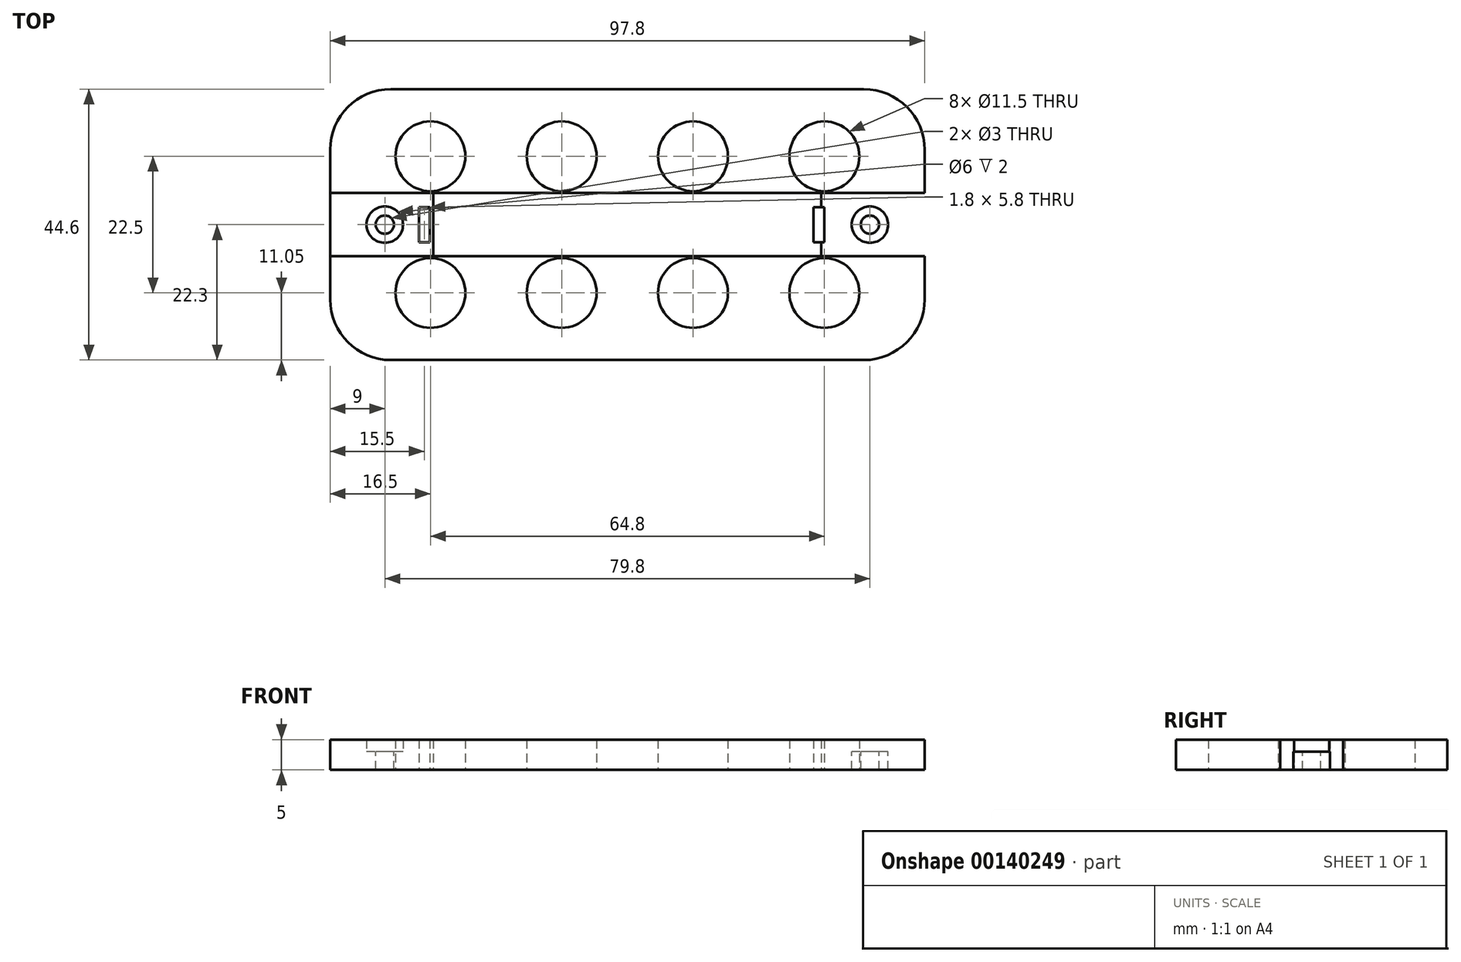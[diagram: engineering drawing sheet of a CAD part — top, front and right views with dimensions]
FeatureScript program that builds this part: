
annotation { "Feature Type Name" : "Feature", "Feature Type Description" : "" }
export const myFeature = defineFeature(function(context is Context, id is Id, definition is map)
    precondition{}
    {
        {
            var Q0;
            Q0=qCreatedBy(makeId("Top.planeOp"),FACE);
            var sketch = newSketch(context, id + "F0", { "sketchPlane" : qUnion([Q0])});
            skLineSegment(sketch, "E0", {"start": v(-3.6, 10.25) * mm, "end": v(18, 10.25) * mm});
            skLineSegment(sketch, "E1", {"start": v(-3.6, 10.25) * mm, "end": v(-25.2, 10.25) * mm});
            skLineSegment(sketch, "E2", {"start": v(-3.6, 0) * mm, "end": v(-3.6, -10.25) * mm});
            skLineSegment(sketch, "E3", {"start": v(-3.6, -10.25) * mm, "end": v(-25.2, -10.25) * mm});
            skLineSegment(sketch, "E4", {"start": v(-3.6, -10.25) * mm, "end": v(18, -10.25) * mm});
            skLineSegment(sketch, "E5.0", {"start": v(-3.6, 11.25) * mm, "end": v(-25.2, 11.25) * mm});
            skLineSegment(sketch, "E5.1", {"start": v(-3.6, 11.25) * mm, "end": v(18, 11.25) * mm});
            skLineSegment(sketch, "E6.0", {"start": v(-3.6, -11.25) * mm, "end": v(18, -11.25) * mm});
            skLineSegment(sketch, "E6.1", {"start": v(-3.6, -11.25) * mm, "end": v(-25.2, -11.25) * mm});
            skLineSegment(sketch, "E7", {"start": v(18, -11.25) * mm, "end": v(39.6, -11.25) * mm});
            skLineSegment(sketch, "E8", {"start": v(18, 11.25) * mm, "end": v(39.6, 11.25) * mm});
            skLineSegment(sketch, "E9", {"start": v(7.2, 11.25) * mm, "end": v(7.2, 0) * mm});
            skLineSegment(sketch, "E10.bottom", {"start": v(-41.7, 22.3) * mm, "end": v(56.1, 22.3) * mm});
            skLineSegment(sketch, "E10.top", {"start": v(-41.7, -22.3) * mm, "end": v(56.1, -22.3) * mm});
            skLineSegment(sketch, "E10.left", {"start": v(-41.7, 22.3) * mm, "end": v(-41.7, -22.3) * mm});
            skLineSegment(sketch, "E10.right", {"start": v(56.1, 22.3) * mm, "end": v(56.1, -22.3) * mm});
            skPoint(sketch, "E10.middle", {"position": v(7.2, 0) * mm});
            skCircle(sketch, "E11", {"center": v(-25.2, 11.25) * mm, "radius": 5.75 * mm});
            skCircle(sketch, "E12", {"center": v(-3.6, 11.25) * mm, "radius": 5.75 * mm});
            skCircle(sketch, "E13", {"center": v(18, 11.25) * mm, "radius": 5.75 * mm});
            skCircle(sketch, "E14", {"center": v(39.6, 11.25) * mm, "radius": 5.75 * mm});
            skCircle(sketch, "E15", {"center": v(-25.2, -11.25) * mm, "radius": 5.75 * mm});
            skCircle(sketch, "E16", {"center": v(-3.6, -11.25) * mm, "radius": 5.75 * mm});
            skCircle(sketch, "E17", {"center": v(18, -11.25) * mm, "radius": 5.75 * mm});
            skCircle(sketch, "E18", {"center": v(39.6, -11.25) * mm, "radius": 5.75 * mm});
            skLineSegment(sketch, "E19", {"start": v(56.1, 0) * mm, "end": v(56.1, -5.2) * mm});
            skLineSegment(sketch, "E20", {"start": v(56.1, 0) * mm, "end": v(56.1, 5.2) * mm});
            skLineSegment(sketch, "E21", {"start": v(56.1, 5.2) * mm, "end": v(-41.7, 5.2) * mm});
            skLineSegment(sketch, "E22", {"start": v(56.1, -5.2) * mm, "end": v(-41.7, -5.2) * mm});
            skLineSegment(sketch, "E23", {"start": v(-41.7, 0) * mm, "end": v(-32.7, 0) * mm});
            skCircle(sketch, "E24", {"center": v(-32.7, 0) * mm, "radius": 3 * mm});
            skCircle(sketch, "E25", {"center": v(-32.7, 0) * mm, "radius": 1.5 * mm});
            skLineSegment(sketch, "E26", {"start": v(56.1, 0) * mm, "end": v(47.1, 0) * mm});
            skCircle(sketch, "E27", {"center": v(47.1, 0) * mm, "radius": 3 * mm});
            skCircle(sketch, "E28", {"center": v(47.1, 0) * mm, "radius": 1.5 * mm});
            skLineSegment(sketch, "E29", {"start": v(-41.7, -5.2) * mm, "end": v(-25.2, -5.2) * mm});
            skLineSegment(sketch, "E30", {"start": v(56.1, 5.2) * mm, "end": v(39.6, 5.2) * mm});
            skLineSegment(sketch, "E31", {"start": v(-41.7, -5.2) * mm, "end": v(-24.7, -5.2) * mm});
            skLineSegment(sketch, "E32", {"start": v(-24.7, -5.2) * mm, "end": v(-24.7, 5.2) * mm});
            skLineSegment(sketch, "E33", {"start": v(56.1, -5.2) * mm, "end": v(39.1, -5.2) * mm});
            skLineSegment(sketch, "E34", {"start": v(39.1, -5.2) * mm, "end": v(39.1, 5.2) * mm});
            skLineSegment(sketch, "E35", {"start": v(-41.7, 0) * mm, "end": v(-27.1, 0) * mm});
            skLineSegment(sketch, "E36", {"start": v(-27.1, 0) * mm, "end": v(-27.1, 2.9) * mm});
            skLineSegment(sketch, "E37", {"start": v(-27.1, 2.9) * mm, "end": v(-25.3, 2.9) * mm});
            skLineSegment(sketch, "E38", {"start": v(-25.3, 2.9) * mm, "end": v(-25.3, -2.9) * mm});
            skLineSegment(sketch, "E39", {"start": v(-25.3, -2.9) * mm, "end": v(-27.1, -2.9) * mm});
            skLineSegment(sketch, "E40", {"start": v(-27.1, -2.9) * mm, "end": v(-27.1, 0) * mm});
            skLineSegment(sketch, "E41", {"start": v(56.1, 0) * mm, "end": v(39.6, 0) * mm});
            skLineSegment(sketch, "E42", {"start": v(39.6, 0) * mm, "end": v(39.6, 2.9) * mm});
            skLineSegment(sketch, "E43", {"start": v(39.6, 2.9) * mm, "end": v(37.8, 2.9) * mm});
            skLineSegment(sketch, "E44", {"start": v(37.8, 2.9) * mm, "end": v(37.8, -2.9) * mm});
            skLineSegment(sketch, "E45", {"start": v(37.8, -2.9) * mm, "end": v(39.6, -2.9) * mm});
            skLineSegment(sketch, "E46", {"start": v(39.6, -2.9) * mm, "end": v(39.6, 0) * mm});
            skSolve(sketch);
        }
        {
            var Q0;
            Q0=makeQuery(id+"F0.imprint","IMPRINT",FACE,{"disambiguationData":[TD([[makeQuery(id+"F0.imprint","IMPRINT",EDGE,{"derivedFrom":sQuery(id+"F0.wireOp",EDGE,"E10.bottom")}),-1.0]])]});
            var Q1;
            {var subQ0=sQuery(id+"F0.wireOp",EDGE,"f6887ee9-049f-47f7-8b07-7ff9263f95ff");var subQ1=makeQuery(id+"F0.imprint","INTERSECT",VERTEX,{"derivedFrom":[sQuery(id+"F0.wireOp",EDGE,"E3"),subQ0]});Q1=makeQuery(id+"F0.imprint","IMPRINT",FACE,{"disambiguationData":[TD([[makeQuery(id+"F0.imprint","IMPRINT",EDGE,{"disambiguationData":[TD([[subQ1,-1.0]])],"derivedFrom":subQ0}),1.0]])]});}
            var Q2;
            {var subQ0=sQuery(id+"F0.wireOp",EDGE,"7b2065db-7b24-4620-b89c-c6dd7d309109");var subQ1=makeQuery(id+"F0.imprint","INTERSECT",VERTEX,{"derivedFrom":[sQuery(id+"F0.wireOp",EDGE,"E1"),subQ0]});Q2=makeQuery(id+"F0.imprint","IMPRINT",FACE,{"disambiguationData":[TD([[makeQuery(id+"F0.imprint","IMPRINT",EDGE,{"disambiguationData":[TD([[subQ1,-1.0]])],"derivedFrom":subQ0}),1.0]])]});}
            var Q3;
            {var subQ1=sQuery(id+"F0.wireOp",EDGE,"4b9a3b46-39bf-4a7f-935b-aec41dfed67a");var subQ3=sQuery(id+"F0.wireOp",EDGE,"3ee279bb-5b09-4dd3-93a1-242deb24ec6a");var subQ4=makeQuery(id+"F0.imprint","INTERSECT",VERTEX,{"derivedFrom":[subQ1,subQ3]});Q3=makeQuery(id+"F0.imprint","IMPRINT",FACE,{"disambiguationData":[TD([[makeQuery(id+"F0.imprint","IMPRINT",EDGE,{"disambiguationData":[TD([[subQ4,1.0]])],"derivedFrom":subQ3}),1.0]])]});}
            var Q4;
            {var subQ0=sQuery(id+"F0.wireOp",EDGE,"4c88f515-e4cd-4761-96bb-9e012f7b4129");var subQ1=makeQuery(id+"F0.imprint","INTERSECT",VERTEX,{"derivedFrom":[sQuery(id+"F0.wireOp",EDGE,"E0"),subQ0]});Q4=makeQuery(id+"F0.imprint","IMPRINT",FACE,{"disambiguationData":[TD([[makeQuery(id+"F0.imprint","IMPRINT",EDGE,{"disambiguationData":[TD([[subQ1,1.0]])],"derivedFrom":subQ0}),1.0]])]});}
            var Q5;
            {var subQ0=sQuery(id+"F0.wireOp",EDGE,"98f43cb8-49ac-4cd2-891b-843e99cd508c");var subQ1=makeQuery(id+"F0.imprint","INTERSECT",VERTEX,{"derivedFrom":[sQuery(id+"F0.wireOp",EDGE,"E4"),subQ0]});Q5=makeQuery(id+"F0.imprint","IMPRINT",FACE,{"disambiguationData":[TD([[makeQuery(id+"F0.imprint","IMPRINT",EDGE,{"disambiguationData":[TD([[subQ1,-1.0]])],"derivedFrom":subQ0}),1.0]])]});}
            var Q6;
            {var subQ1=sQuery(id+"F0.wireOp",EDGE,"4b9a3b46-39bf-4a7f-935b-aec41dfed67a");var subQ3=sQuery(id+"F0.wireOp",EDGE,"3ee279bb-5b09-4dd3-93a1-242deb24ec6a");var subQ4=makeQuery(id+"F0.imprint","INTERSECT",VERTEX,{"derivedFrom":[subQ1,subQ3]});Q6=makeQuery(id+"F0.imprint","IMPRINT",FACE,{"disambiguationData":[TD([[makeQuery(id+"F0.imprint","IMPRINT",EDGE,{"disambiguationData":[TD([[subQ4,-1.0]])],"derivedFrom":subQ3}),1.0]])]});}
            var Q7;
            {var subQ3=sQuery(id+"F0.wireOp",EDGE,"3ee279bb-5b09-4dd3-93a1-242deb24ec6a");var subQ5=sQuery(id+"F0.wireOp",EDGE,"E5.1");var subQ8=makeQuery(id+"F0.imprint","INTERSECT",VERTEX,{"derivedFrom":[subQ3,subQ5]});Q7=makeQuery(id+"F0.imprint","IMPRINT",FACE,{"disambiguationData":[TD([[makeQuery(id+"F0.imprint","IMPRINT",EDGE,{"disambiguationData":[TD([[subQ8,1.0]])],"derivedFrom":subQ3}),1.0]])]});}
            var Q8;
            {var subQ0=sQuery(id+"F0.wireOp",EDGE,"E5.1");var subQ1=sQuery(id+"F0.wireOp",EDGE,"3ee279bb-5b09-4dd3-93a1-242deb24ec6a");var subQ2=makeQuery(id+"F0.imprint","INTERSECT",VERTEX,{"derivedFrom":[subQ1,subQ0]});Q8=makeQuery(id+"F0.imprint","IMPRINT",FACE,{"disambiguationData":[TD([[makeQuery(id+"F0.imprint","IMPRINT",EDGE,{"disambiguationData":[TD([[subQ2,-1.0]])],"derivedFrom":subQ1}),1.0]])]});}
            var Q9;
            {var subQ0=sQuery(id+"F0.wireOp",EDGE,"E8");var subQ1=sQuery(id+"F0.wireOp",EDGE,"4c88f515-e4cd-4761-96bb-9e012f7b4129");var subQ2=makeQuery(id+"F0.imprint","INTERSECT",VERTEX,{"derivedFrom":[subQ1,subQ0]});Q9=makeQuery(id+"F0.imprint","IMPRINT",FACE,{"disambiguationData":[TD([[makeQuery(id+"F0.imprint","IMPRINT",EDGE,{"disambiguationData":[TD([[subQ2,-1.0]])],"derivedFrom":subQ1}),1.0]])]});}
            var Q10;
            {var subQ0=sQuery(id+"F0.wireOp",EDGE,"E6.1");var subQ1=sQuery(id+"F0.wireOp",EDGE,"78d3df8a-ec91-46e3-93df-5ccd42c28f7d");var subQ2=makeQuery(id+"F0.imprint","INTERSECT",VERTEX,{"derivedFrom":[subQ1,subQ0]});Q10=makeQuery(id+"F0.imprint","IMPRINT",FACE,{"disambiguationData":[TD([[makeQuery(id+"F0.imprint","IMPRINT",EDGE,{"disambiguationData":[TD([[subQ2,-1.0]])],"derivedFrom":subQ1}),1.0]])]});}
            var Q11;
            {var subQ0=sQuery(id+"F0.wireOp",EDGE,"E7");var subQ1=sQuery(id+"F0.wireOp",EDGE,"98f43cb8-49ac-4cd2-891b-843e99cd508c");var subQ2=makeQuery(id+"F0.imprint","INTERSECT",VERTEX,{"derivedFrom":[subQ1,subQ0]});Q11=makeQuery(id+"F0.imprint","IMPRINT",FACE,{"disambiguationData":[TD([[makeQuery(id+"F0.imprint","IMPRINT",EDGE,{"disambiguationData":[TD([[subQ2,1.0]])],"derivedFrom":subQ1}),1.0]])]});}
            var Q12;
            {var subQ0=sQuery(id+"F0.wireOp",EDGE,"E9");var subQ1=sQuery(id+"F0.wireOp",EDGE,"E0");var subQ2=makeQuery(id+"F0.imprint","INTERSECT",VERTEX,{"derivedFrom":[subQ1,subQ0]});Q12=makeQuery(id+"F0.imprint","IMPRINT",FACE,{"disambiguationData":[TD([[makeQuery(id+"F0.imprint","IMPRINT",EDGE,{"disambiguationData":[TD([[subQ2,-1.0]])],"derivedFrom":subQ1}),1.0]])]});}
            var Q13;
            {var subQ1=sQuery(id+"F0.wireOp",EDGE,"E2");var subQ3=sQuery(id+"F0.wireOp",EDGE,"78d3df8a-ec91-46e3-93df-5ccd42c28f7d");var subQ4=makeQuery(id+"F0.imprint","INTERSECT",VERTEX,{"derivedFrom":[subQ1,subQ3]});Q13=makeQuery(id+"F0.imprint","IMPRINT",FACE,{"disambiguationData":[TD([[makeQuery(id+"F0.imprint","IMPRINT",EDGE,{"disambiguationData":[TD([[subQ4,-1.0]])],"derivedFrom":subQ3}),1.0]])]});}
            var Q14;
            {var subQ0=sQuery(id+"F0.wireOp",EDGE,"E9");var subQ1=sQuery(id+"F0.wireOp",EDGE,"E0");var subQ2=makeQuery(id+"F0.imprint","INTERSECT",VERTEX,{"derivedFrom":[subQ1,subQ0]});Q14=makeQuery(id+"F0.imprint","IMPRINT",FACE,{"disambiguationData":[TD([[makeQuery(id+"F0.imprint","IMPRINT",EDGE,{"disambiguationData":[TD([[subQ2,-1.0]])],"derivedFrom":subQ1}),1.0]])]});}
            var Q15;
            {var subQ0=sQuery(id+"F0.wireOp",EDGE,"E5.1");var subQ1=sQuery(id+"F0.wireOp",EDGE,"3ee279bb-5b09-4dd3-93a1-242deb24ec6a");var subQ2=makeQuery(id+"F0.imprint","INTERSECT",VERTEX,{"derivedFrom":[subQ1,subQ0]});Q15=makeQuery(id+"F0.imprint","IMPRINT",FACE,{"disambiguationData":[TD([[makeQuery(id+"F0.imprint","IMPRINT",EDGE,{"disambiguationData":[TD([[subQ2,1.0]])],"derivedFrom":subQ1}),-1.0]])]});}
            var Q16;
            {var subQ0=sQuery(id+"F0.wireOp",EDGE,"E5.0");var subQ1=sQuery(id+"F0.wireOp",EDGE,"3ee279bb-5b09-4dd3-93a1-242deb24ec6a");var subQ2=makeQuery(id+"F0.imprint","INTERSECT",VERTEX,{"derivedFrom":[subQ1,subQ0]});Q16=makeQuery(id+"F0.imprint","IMPRINT",FACE,{"disambiguationData":[TD([[makeQuery(id+"F0.imprint","IMPRINT",EDGE,{"disambiguationData":[TD([[subQ2,-1.0]])],"derivedFrom":subQ1}),-1.0]])]});}
            var Q17;
            {var subQ0=sQuery(id+"F0.wireOp",EDGE,"f6887ee9-049f-47f7-8b07-7ff9263f95ff");var subQ1=sQuery(id+"F0.wireOp",EDGE,"E3");var subQ2=makeQuery(id+"F0.imprint","INTERSECT",VERTEX,{"derivedFrom":[subQ1,subQ0]});Q17=makeQuery(id+"F0.imprint","IMPRINT",FACE,{"disambiguationData":[TD([[makeQuery(id+"F0.imprint","IMPRINT",EDGE,{"disambiguationData":[TD([[subQ2,1.0]])],"derivedFrom":subQ1}),1.0]])]});}
            var Q18;
            {var subQ1=sQuery(id+"F0.wireOp",EDGE,"E2");var subQ3=sQuery(id+"F0.wireOp",EDGE,"78d3df8a-ec91-46e3-93df-5ccd42c28f7d");var subQ4=makeQuery(id+"F0.imprint","INTERSECT",VERTEX,{"derivedFrom":[subQ1,subQ3]});Q18=makeQuery(id+"F0.imprint","IMPRINT",FACE,{"disambiguationData":[TD([[makeQuery(id+"F0.imprint","IMPRINT",EDGE,{"disambiguationData":[TD([[subQ4,1.0]])],"derivedFrom":subQ3}),1.0]])]});}
            var Q19;
            {var subQ0=sQuery(id+"F0.wireOp",EDGE,"78d3df8a-ec91-46e3-93df-5ccd42c28f7d");var subQ5=sQuery(id+"F0.wireOp",EDGE,"E3");var subQ6=makeQuery(id+"F0.imprint","INTERSECT",VERTEX,{"derivedFrom":[subQ5,subQ0]});Q19=makeQuery(id+"F0.imprint","IMPRINT",FACE,{"disambiguationData":[TD([[makeQuery(id+"F0.imprint","IMPRINT",EDGE,{"disambiguationData":[TD([[subQ6,-1.0]])],"derivedFrom":subQ0}),1.0]])]});}
            var Q20;
            {var subQ0=sQuery(id+"F0.wireOp",EDGE,"98f43cb8-49ac-4cd2-891b-843e99cd508c");var subQ1=sQuery(id+"F0.wireOp",EDGE,"E4");var subQ2=makeQuery(id+"F0.imprint","INTERSECT",VERTEX,{"derivedFrom":[subQ1,subQ0]});Q20=makeQuery(id+"F0.imprint","IMPRINT",FACE,{"disambiguationData":[TD([[makeQuery(id+"F0.imprint","IMPRINT",EDGE,{"disambiguationData":[TD([[subQ2,1.0]])],"derivedFrom":subQ1}),-1.0]])]});}
            var Q21;
            {var subQ0=sQuery(id+"F0.wireOp",EDGE,"E9");var subQ1=sQuery(id+"F0.wireOp",EDGE,"E0");var subQ2=makeQuery(id+"F0.imprint","INTERSECT",VERTEX,{"derivedFrom":[subQ1,subQ0]});Q21=makeQuery(id+"F0.imprint","IMPRINT",FACE,{"disambiguationData":[TD([[makeQuery(id+"F0.imprint","IMPRINT",EDGE,{"disambiguationData":[TD([[subQ2,1.0]])],"derivedFrom":subQ1}),1.0]])]});}
            var Q22;
            {var subQ0=sQuery(id+"F0.wireOp",EDGE,"E11");var subQ1=sQuery(id+"F0.wireOp",EDGE,"E1");var subQ2=makeQuery(id+"F0.imprint","INTERSECT",VERTEX,{"derivedFrom":[subQ1,subQ0]});Q22=makeQuery(id+"F0.imprint","IMPRINT",FACE,{"disambiguationData":[TD([[makeQuery(id+"F0.imprint","IMPRINT",EDGE,{"disambiguationData":[TD([[subQ2,1.0]])],"derivedFrom":subQ1}),-1.0]])]});}
            var Q23;
            {var subQ8=sQuery(id+"F0.wireOp",EDGE,"E10.top");Q23=makeQuery(id+"F0.imprint","IMPRINT",FACE,{"disambiguationData":[TD([[makeQuery(id+"F0.imprint","IMPRINT",EDGE,{"derivedFrom":subQ8}),1.0]])]});}
            var Q24;
            {var subQ1=sQuery(id+"F0.wireOp",EDGE,"4b9a3b46-39bf-4a7f-935b-aec41dfed67a");var subQ5=sQuery(id+"F0.wireOp",EDGE,"E21");var subQ9=makeQuery(id+"F0.imprint","INTERSECT",VERTEX,{"derivedFrom":[subQ1,subQ5]});Q24=makeQuery(id+"F0.imprint","IMPRINT",FACE,{"disambiguationData":[TD([[makeQuery(id+"F0.imprint","IMPRINT",EDGE,{"disambiguationData":[TD([[subQ9,-1.0]])],"derivedFrom":subQ1}),-1.0]])]});}
            var Q25;
            Q25=makeQuery(id+"F0.imprint","IMPRINT",FACE,{"disambiguationData":[TD([[makeQuery(id+"F0.imprint","IMPRINT",EDGE,{"derivedFrom":sQuery(id+"F0.wireOp",EDGE,"E36")}),-1.0]])]});
            var Q26;
            Q26=makeQuery(id+"F0.imprint","IMPRINT",FACE,{"disambiguationData":[TD([[makeQuery(id+"F0.imprint","IMPRINT",EDGE,{"derivedFrom":sQuery(id+"F0.wireOp",EDGE,"da98e559-8631-45a9-bd82-e2b8f23b4d3f0.MirrorCS")}),1.0]])]});
            var Q27;
            {var subQ5=sQuery(id+"F0.wireOp",EDGE,"E44");Q27=makeQuery(id+"F0.imprint","IMPRINT",FACE,{"disambiguationData":[TD([[makeQuery(id+"F0.imprint","IMPRINT",EDGE,{"derivedFrom":subQ5}),1.0]])]});}
            var Q28;
            {var subQ5=sQuery(id+"F0.wireOp",EDGE,"E42");Q28=makeQuery(id+"F0.imprint","IMPRINT",FACE,{"disambiguationData":[TD([[makeQuery(id+"F0.imprint","IMPRINT",EDGE,{"derivedFrom":subQ5}),1.0]])]});}
            extrude(context, id + "F1", {"entities" : qUnion([Q0, Q1, Q2, Q3, Q4, Q5, Q6, Q7, Q8, Q9, Q10, Q11, Q12, Q13, Q14, Q15, Q16, Q17, Q18, Q19, Q20, Q21, Q22, Q23, Q24, Q25, Q26, Q27, Q28]), "endBound" : BoundingType.SYMMETRIC, "depth" : 5 * mm});
        }
        {
            var Q0;
            {var subQ6=sQuery(id+"F0.wireOp",EDGE,"E19");Q0=makeQuery(id+"F0.imprint","IMPRINT",FACE,{"disambiguationData":[TD([[makeQuery(id+"F0.imprint","IMPRINT",EDGE,{"derivedFrom":subQ6}),-1.0]])]});}
            var Q1;
            Q1=makeQuery(id+"F0.imprint","IMPRINT",FACE,{"disambiguationData":[TD([[makeQuery(id+"F0.imprint","IMPRINT",EDGE,{"derivedFrom":sQuery(id+"F0.wireOp",EDGE,"E24")}),-1.0]])]});
            var Q2;
            {var subQ11=sQuery(id+"F0.wireOp",EDGE,"E20");Q2=makeQuery(id+"F0.imprint","IMPRINT",FACE,{"disambiguationData":[TD([[makeQuery(id+"F0.imprint","IMPRINT",EDGE,{"derivedFrom":subQ11}),1.0]])]});}
            extrude(context, id + "F2", {"entities" : qUnion([Q0, Q1, Q2]), "depth" : 2.5 * mm});
        }
        {
            var Q0;
            {var subQ6=sQuery(id+"F0.wireOp",EDGE,"E19");Q0=makeQuery(id+"F0.imprint","IMPRINT",FACE,{"disambiguationData":[TD([[makeQuery(id+"F0.imprint","IMPRINT",EDGE,{"derivedFrom":subQ6}),-1.0]])]});}
            var Q1;
            Q1=makeQuery(id+"F0.imprint","IMPRINT",FACE,{"disambiguationData":[TD([[makeQuery(id+"F0.imprint","IMPRINT",EDGE,{"derivedFrom":sQuery(id+"F0.wireOp",EDGE,"E24")}),-1.0]])]});
            var Q2;
            {var subQ11=sQuery(id+"F0.wireOp",EDGE,"E20");Q2=makeQuery(id+"F0.imprint","IMPRINT",FACE,{"disambiguationData":[TD([[makeQuery(id+"F0.imprint","IMPRINT",EDGE,{"derivedFrom":subQ11}),1.0]])]});}
            extrude(context, id + "F3", {"entities" : qUnion([Q0, Q1, Q2]), "oppositeDirection" : true, "depth" : 2.5 * mm});
        }
        {
            var Q0;
            Q0=makeQuery(id+"F1.opExtrude","SWEPT_EDGE",EDGE,{"disambiguationData":[OSD([sQuery(id+"F0.wireOp",EDGE,"E10.top"),sQuery(id+"F0.wireOp",EDGE,"E10.right")])]});
            var Q1;
            Q1=makeQuery(id+"F1.opExtrude","SWEPT_EDGE",EDGE,{"disambiguationData":[OSD([sQuery(id+"F0.wireOp",EDGE,"E10.top"),sQuery(id+"F0.wireOp",EDGE,"E10.left")])]});
            var Q2;
            Q2=makeQuery(id+"F1.opExtrude","SWEPT_EDGE",EDGE,{"disambiguationData":[OSD([sQuery(id+"F0.wireOp",EDGE,"E10.bottom"),sQuery(id+"F0.wireOp",EDGE,"E10.left")])]});
            var Q3;
            Q3=makeQuery(id+"F1.opExtrude","SWEPT_EDGE",EDGE,{"disambiguationData":[OSD([sQuery(id+"F0.wireOp",EDGE,"E10.bottom"),sQuery(id+"F0.wireOp",EDGE,"E10.right")])]});
            fillet(context, id + "F4", {"entities" : qUnion([Q0, Q1, Q2, Q3]), "radius" : 10 * mm, "tangentPropagation" : true, "allowEdgeOverflow" : false});
        }
        {
            var Q0;
            Q0=makeQuery(id+"F0.imprint","IMPRINT",FACE,{"disambiguationData":[TD([[makeQuery(id+"F0.imprint","IMPRINT",EDGE,{"derivedFrom":sQuery(id+"F0.wireOp",EDGE,"E24")}),1.0]])]});
            var Q1;
            Q1=makeQuery(id+"F0.imprint","IMPRINT",FACE,{"disambiguationData":[TD([[makeQuery(id+"F0.imprint","IMPRINT",EDGE,{"derivedFrom":sQuery(id+"F0.wireOp",EDGE,"E27")}),1.0]])]});
            extrude(context, id + "F5", {"entities" : qUnion([Q0, Q1]), "operationType" : NewBodyOperationType.ADD, "oppositeDirection" : true, "depth" : 2.5 * mm, "hasSecondDirection" : true, "secondDirectionOppositeDirection" : false, "secondDirectionDepth" : 0.5 * mm});
        }
        {
            var Q0;
            {var subQ0=sQuery(id+"F0.wireOp",EDGE,"CT9pdsSq-TdKI-GGn8-ivA1-mKq1e7lIbSY2");Q0=makeQuery(id+"F0.imprint","IMPRINT",FACE,{"disambiguationData":[TD([[makeQuery(id+"F0.imprint","IMPRINT",EDGE,{"derivedFrom":subQ0}),-1.0]])]});}
            var Q1;
            {var subQ4=sQuery(id+"F0.wireOp",EDGE,"SJNfEovD-iz4o-dpNM-rAGv-JnHJXBV6g93F");Q1=makeQuery(id+"F0.imprint","IMPRINT",FACE,{"disambiguationData":[TD([[makeQuery(id+"F0.imprint","IMPRINT",EDGE,{"derivedFrom":subQ4}),-1.0]])]});}
            var Q2;
            {var subQ0=sQuery(id+"F0.wireOp",EDGE,"E32");Q2=makeQuery(id+"F0.imprint","IMPRINT",FACE,{"disambiguationData":[TD([[makeQuery(id+"F0.imprint","IMPRINT",EDGE,{"derivedFrom":subQ0}),-1.0]])]});}
            extrude(context, id + "F6", {"entities" : qUnion([Q0, Q1, Q2]), "endBound" : BoundingType.SYMMETRIC, "depth" : 5 * mm});
        }
    });
